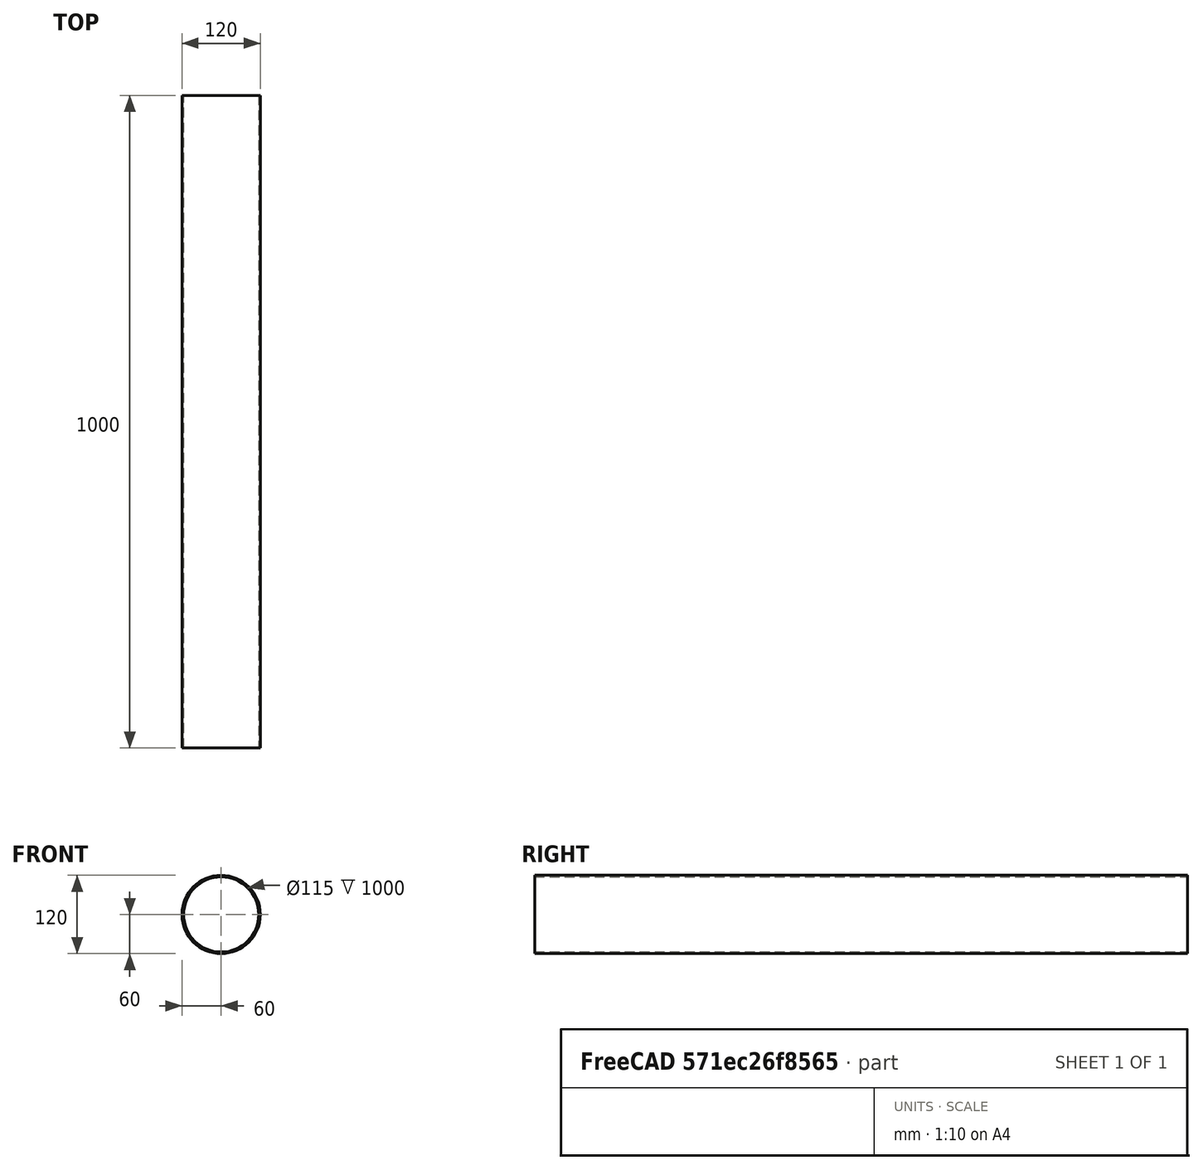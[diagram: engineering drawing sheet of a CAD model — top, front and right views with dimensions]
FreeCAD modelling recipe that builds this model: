
FCSTD DOCUMENT  (FreeCAD 1.0R39285 (Git))
Label: pipe4
License: All rights reserved
LicenseURL: https://en.wikipedia.org/wiki/All_rights_reserved
objects: Sketcher::SketchObject×1, PartDesign::Pad×1, PartDesign::Body×1
note: 6 computed .brp shape members not serialized (recipe doc carries the construction recipe); baked Part::Feature solids carry a one-line shape summary decoded from their .brp

FEATURE [Sketcher::SketchObject] Sketch
  ArcFitTolerance = 1e-06
  AttachmentSupport = -> [XZ_Plane]
  FullyConstrained = true
  MakeInternals = false
  MapMode = 5
  Placement = pos=(0,0,0) rot=(1,0,0;1.5708rad)
  sketch-geometry (2):
    g0: Circle CenterX=0 CenterY=0 CenterZ=0 NormalX=0 NormalY=0 NormalZ=1 AngleXU=0 Radius=60
    g1: Circle CenterX=0 CenterY=0 CenterZ=0 NormalX=0 NormalY=0 NormalZ=1 AngleXU=0 Radius=57.5
  constraints (4):
    c: Coincident(g0,g-1)
    c: Diameter(g0) = 120
    c: Coincident(g1,g0)
    c: Diameter(g1) = 115
FEATURE [PartDesign::Pad] Pad
  Direction = (0,-1,2e-16)
  Length = 1000
  Length2 = 10
  Placement = pos=(0,0,0) rot=(1,0,0;1.5708rad)
  Profile = -> Sketch
  ReferenceAxis = -> Sketch [N_Axis]
  Refine = true
  Suppressed = false
  Type = 0
FEATURE [PartDesign::Body] Body
  AllowCompound = false
  Group = -> [Sketch,Pad]
  Origin = -> Origin
  Tip = -> Pad
